# Revit family: CENTUM Profilverbinder
name_source: partatom
category: HLS-Bauteile
revit_build: Autodesk Revit 2017 (Build: 20190507_1515(x64)
units: mm (PartAtom-declared; Revit-internal decimal feet)

## family parameters
Arbeitsebenenbasiert = Ja
Beim Laden mit Abzugskörper schneiden = Nein
Bemaßung runder Anschluss = Durchmesser verwenden
Gemeinsam genutzt = Ja
Immer vertikal = Nein
Raumberechnungspunkt = Nein
Teiletyp = Normal

## types (4) — shared parameters
Fabrikat = MEFA
Firma = MEFA Befestigungs- und Montagesysteme GmbH
Langloch = 14x40 mm
Lieferumfang = 2 x U-Stahl, 8 x Hammerkopfschraube, gezahnt M12/40
Material = Stahl
Materialname = S235
Mengeneinheit = St
Oberflaeche = feuerstückverzinkt
Oberfläche Schraube = Zink-Nickel
Profil = CENTUM
Vorgabe-Ansicht = 1219 mm
vpe = 1 St

## per-type parameters (varying)
| type | A | Artikelnummer | B | Breite | EAN | Gewicht | Gewicht pro Bauteil | Höhe | Kurztext1 | Kurztext2 | Profiltyp | U-Stahl |
| CENTUM Profilverbinder XL 80 | 75 mm | 1640805010 | 79 mm | 60 mm  [stored 0.19685 ft] | 4250928458315 | 4.94 kg | 4.94 kg | 30 mm | Profilverbinder CENTUM XL 80 | 380x60x30 mm Lochd. 14x40 mm | XL 80 | U-Stahl mit Lochung : U-Stahl  60x 30x 380  14x40 |
| CENTUM Profilverbinder XL100 | 93 mm  [stored 0.305118 ft] | 1640005010 | 97 mm  [stored 0.318241 ft] | 80 mm  [stored 0.262467 ft] | 4250928436900 | 7.90 kg | 7.90 kg | 45 mm | Profilverbinder CENTUM XL 100, 120, 200 | 380x80x45 mm Lochd. 14x40 mm | XL 100, XL 120, XL 200 | U-Stahl mit Lochung : U-Stahl  80x 45x 380  14x40 |
| CENTUM Profilverbinder XL120 | 112 mm  [stored 0.367454 ft] | 1640005010 | 116 mm  [stored 0.380577 ft] | 80 mm  [stored 0.262467 ft] | 4250928436900 | 7.90 kg | 7.90 kg | 45 mm | Profilverbinder CENTUM XL 100, 120, 200 | 380x80x45 mm Lochd. 14x40 mm | XL 100, XL 120, XL 200 | U-Stahl mit Lochung : U-Stahl  80x 45x 380  14x40 |
| CENTUM Profilverbinder XL200 | 190 mm | 1640005010 | 194 mm  [stored 0.636483 ft] | 80 mm  [stored 0.262467 ft] | 4250928436900 | 7.90 kg | 7.90 kg | 45 mm | Profilverbinder CENTUM XL 100, 120, 200 | 380x80x45 mm Lochd. 14x40 mm | XL 100, XL 120, XL 200 | U-Stahl mit Lochung : U-Stahl  80x 45x 380  14x40 |

note: [stored X ft] marks values corroborated as IEEE doubles in the binary element streams (Revit-internal decimal feet)

## geometry (parser evidence)
native form markers: Sweep x1
no freeform markers — native parametric forms only
